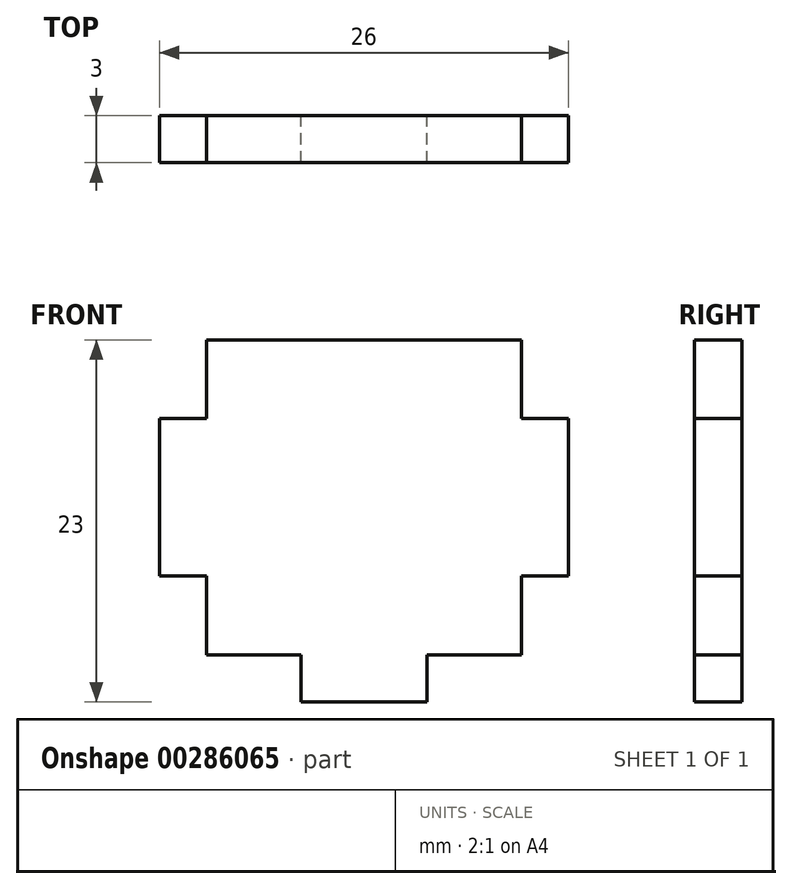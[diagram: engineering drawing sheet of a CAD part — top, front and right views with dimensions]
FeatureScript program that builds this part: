
annotation { "Feature Type Name" : "Feature", "Feature Type Description" : "" }
export const myFeature = defineFeature(function(context is Context, id is Id, definition is map)
    precondition{}
    {
        {
            var Q0;
            Q0=qCreatedBy(makeId("Front.planeOp"),FACE);
            var sketch = newSketch(context, id + "F0", { "sketchPlane" : qUnion([Q0])});
            skLineSegment(sketch, "E0", {"start": v(0, 10) * mm, "end": v(-10, 10) * mm});
            skLineSegment(sketch, "E1", {"start": v(-10, 10) * mm, "end": v(-10, 5) * mm});
            skLineSegment(sketch, "E2", {"start": v(-10, 5) * mm, "end": v(-13, 5) * mm});
            skLineSegment(sketch, "E3", {"start": v(-13, 5) * mm, "end": v(-13, -5) * mm});
            skLineSegment(sketch, "E4", {"start": v(-13, -5) * mm, "end": v(-10, -5) * mm});
            skLineSegment(sketch, "E5", {"start": v(-10, -5) * mm, "end": v(-10, -10) * mm});
            skLineSegment(sketch, "E6", {"start": v(-10, -10) * mm, "end": v(-4, -10) * mm});
            skLineSegment(sketch, "E7", {"start": v(-4, -10) * mm, "end": v(-4, -13) * mm});
            skLineSegment(sketch, "E8", {"start": v(-4, -13) * mm, "end": v(0, -13) * mm});
            skLineSegment(sketch, "E9", {"start": v(-13, 0) * mm, "end": v(0, 0) * mm, "construction": true});
            skLineSegment(sketch, "E10.MirrorCS", {"start": v(0, 10) * mm, "end": v(10, 10) * mm});
            skLineSegment(sketch, "E11.MirrorCS", {"start": v(10, 10) * mm, "end": v(10, 5) * mm});
            skLineSegment(sketch, "E12.MirrorCS", {"start": v(4, -10) * mm, "end": v(4, -13) * mm});
            skLineSegment(sketch, "E13.MirrorCS", {"start": v(4, -13) * mm, "end": v(0, -13) * mm});
            skLineSegment(sketch, "E14.MirrorCS", {"start": v(13, -5) * mm, "end": v(10, -5) * mm});
            skLineSegment(sketch, "E15.MirrorCS", {"start": v(13, 5) * mm, "end": v(13, -5) * mm});
            skLineSegment(sketch, "E16.MirrorCS", {"start": v(10, -10) * mm, "end": v(4, -10) * mm});
            skLineSegment(sketch, "E17.MirrorCS", {"start": v(10, 5) * mm, "end": v(13, 5) * mm});
            skLineSegment(sketch, "E18.MirrorCS", {"start": v(10, -5) * mm, "end": v(10, -10) * mm});
            skSolve(sketch);
        }
        {
            var Q0;
            Q0 = qSketchRegion(id + "F0", true);
            extrude(context, id + "F1", {"entities" : qUnion([Q0]), "depth" : 3 * mm});
        }
    });
